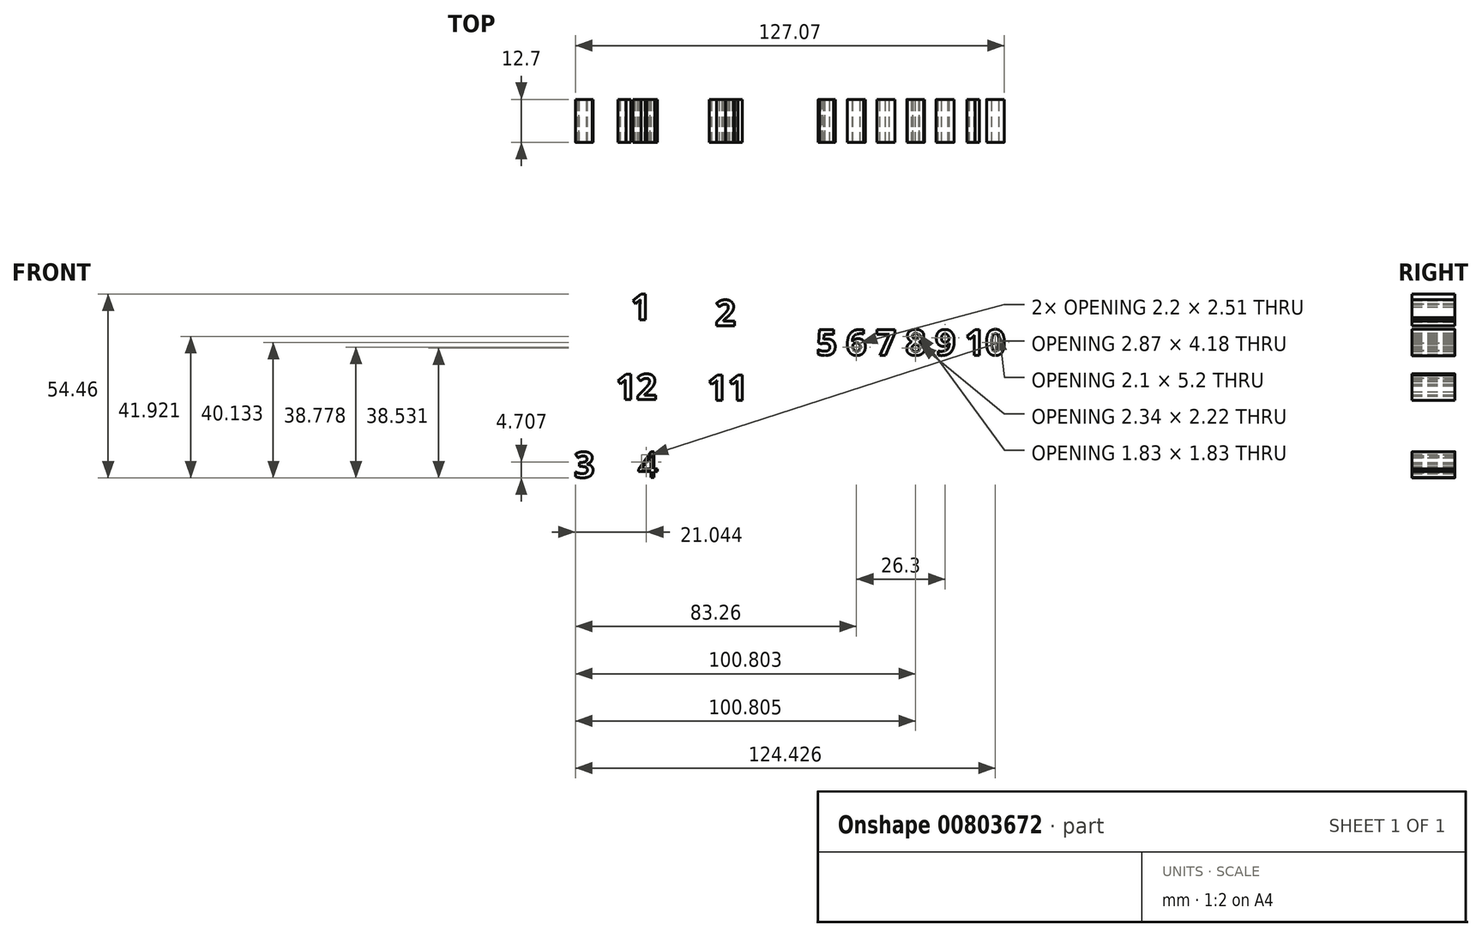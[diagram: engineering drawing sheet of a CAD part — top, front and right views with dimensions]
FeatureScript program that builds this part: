
annotation { "Feature Type Name" : "Feature", "Feature Type Description" : "" }
export const myFeature = defineFeature(function(context is Context, id is Id, definition is map)
    precondition{}
    {
        {
            var Q0;
            Q0=qCreatedBy(makeId("Front.planeOp"),FACE);
            var sketch = newSketch(context, id + "F0", { "sketchPlane" : qUnion([Q0])});
            skText(sketch, "E0", { "text": "1", "fontName": "OpenSans-Bold.ttf"});
            skText(sketch, "E1", { "text": "12", "fontName": "OpenSans-Bold.ttf"});
            skText(sketch, "E2", { "text": "2 ", "fontName": "OpenSans-Bold.ttf"});
            skText(sketch, "E3", { "text": "11", "fontName": "OpenSans-Bold.ttf"});
            skText(sketch, "E4", { "text": "3 ", "fontName": "OpenSans-Bold.ttf"});
            skText(sketch, "E5", { "text": "4", "fontName": "OpenSans-Regular.ttf"});
            skText(sketch, "E6", { "text": "5 6 7 8 9 10", "fontName": "OpenSans-Bold.ttf"});
            const initialGuessF0  = {"E0": [-0.04822, 0.0468, 1, 0, 0.00762], "E1": [-0.05258, 0.02308, 1, 0, 0.00762], "E2": [-0.0232, 0.04503, 1, 0, 0.00762], "E3": [-0.02552, 0.02286, 1, 0, 0.00762], "E4": [-0.065, 0, 1, 0, 0.00762], "E5": [-0.04607, 0, 1, 0, 0.00762], "E6": [0.00681, 0.03625, 1, 0, 0.00762]};
            skSetInitialGuess(sketch, initialGuessF0);
            skSolve(sketch);
        }
        {
            var Q0;
            Q0 = qSketchRegion(id + "F0", true);
            extrude(context, id + "F1", {"entities" : qUnion([Q0]), "depth" : 12.7 * mm, "offsetDistance" : 25.4 * mm});
        }
    });
